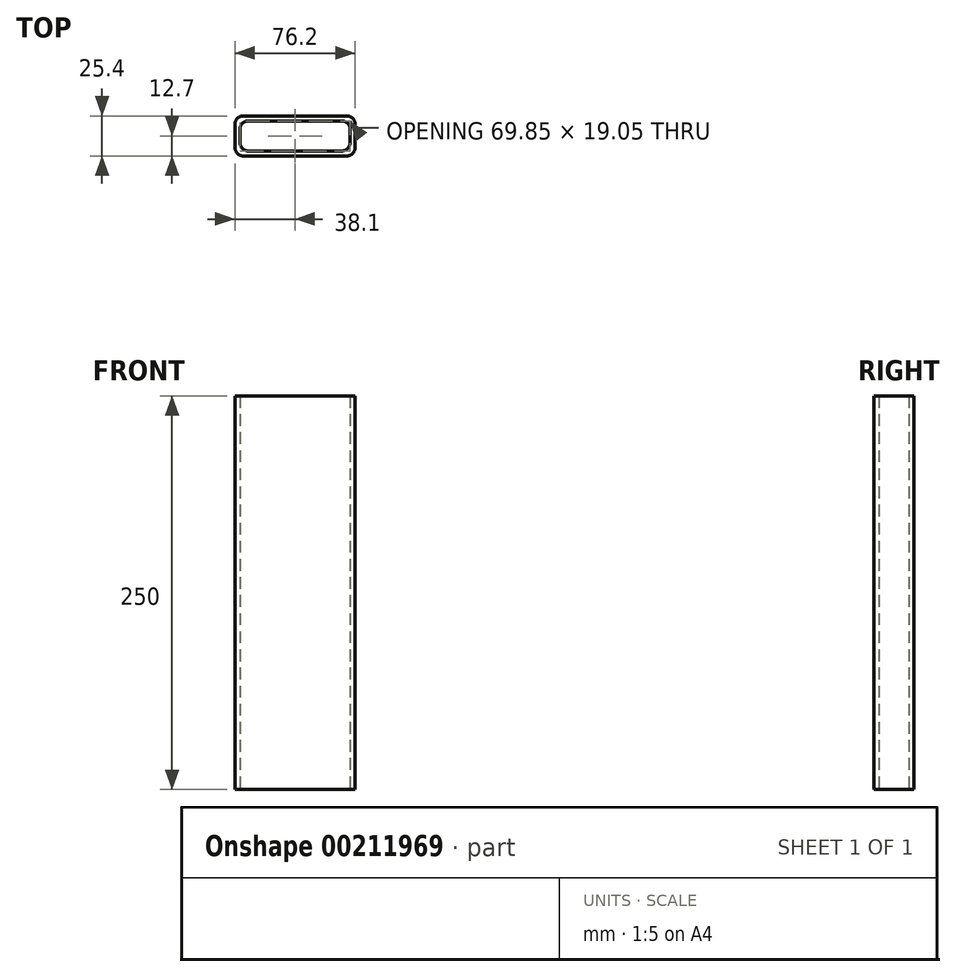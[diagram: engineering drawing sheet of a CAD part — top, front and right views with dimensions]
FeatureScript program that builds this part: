
annotation { "Feature Type Name" : "Feature", "Feature Type Description" : "" }
export const myFeature = defineFeature(function(context is Context, id is Id, definition is map)
    precondition{}
    {
        {
            var Q0;
            Q0=qCreatedBy(makeId("Top.planeOp"),FACE);
            var sketch = newSketch(context, id + "F0", { "sketchPlane" : qUnion([Q0])});
            skLineSegment(sketch, "E0.bottom", {"start": v(38.1, -12.7) * mm, "end": v(-38.1, -12.7) * mm});
            skLineSegment(sketch, "E0.top", {"start": v(38.1, 12.7) * mm, "end": v(-38.1, 12.7) * mm});
            skLineSegment(sketch, "E0.left", {"start": v(38.1, -12.7) * mm, "end": v(38.1, 12.7) * mm});
            skLineSegment(sketch, "E0.right", {"start": v(-38.1, -12.7) * mm, "end": v(-38.1, 12.7) * mm});
            skPoint(sketch, "E0.middle", {"position": v(0, 0) * mm});
            skLineSegment(sketch, "E1.bottom", {"start": v(34.93, -9.52) * mm, "end": v(-34.93, -9.53) * mm});
            skLineSegment(sketch, "E1.top", {"start": v(34.93, 9.53) * mm, "end": v(-34.93, 9.52) * mm});
            skLineSegment(sketch, "E1.left", {"start": v(34.93, -9.52) * mm, "end": v(34.93, 9.53) * mm});
            skLineSegment(sketch, "E1.right", {"start": v(-34.93, -9.53) * mm, "end": v(-34.93, 9.52) * mm});
            skSolve(sketch);
        }
        {
            var Q0;
            Q0=makeQuery(id+"F0.imprint","IMPRINT",FACE,{"disambiguationData":[TD([[makeQuery(id+"F0.imprint","IMPRINT",EDGE,{"derivedFrom":sQuery(id+"F0.wireOp",EDGE,"E0.bottom")}),-1.0]])]});
            extrude(context, id + "F1", {"entities" : qUnion([Q0]), "depth" : 250 * mm});
        }
        {
            var Q0;
            Q0=makeQuery(id+"F1.opExtrude","SWEPT_EDGE",EDGE,{"disambiguationData":[OSD([sQuery(id+"F0.wireOp",EDGE,"E0.bottom"),sQuery(id+"F0.wireOp",EDGE,"E0.left")])]});
            var Q1;
            Q1=makeQuery(id+"F1.opExtrude","SWEPT_EDGE",EDGE,{"disambiguationData":[OSD([sQuery(id+"F0.wireOp",EDGE,"E0.top"),sQuery(id+"F0.wireOp",EDGE,"E0.left")])]});
            var Q2;
            Q2=makeQuery(id+"F1.opExtrude","SWEPT_EDGE",EDGE,{"disambiguationData":[OSD([sQuery(id+"F0.wireOp",EDGE,"E0.bottom"),sQuery(id+"F0.wireOp",EDGE,"E0.right")])]});
            var Q3;
            Q3=makeQuery(id+"F1.opExtrude","SWEPT_EDGE",EDGE,{"disambiguationData":[OSD([sQuery(id+"F0.wireOp",EDGE,"E0.top"),sQuery(id+"F0.wireOp",EDGE,"E0.right")])]});
            fillet(context, id + "F2", {"entities" : qUnion([Q0, Q1, Q2, Q3]), "radius" : 5.08 * mm, "tangentPropagation" : true, "allowEdgeOverflow" : false});
        }
        {
            var Q0;
            Q0=makeQuery(id+"F1.opExtrude","SWEPT_EDGE",EDGE,{"disambiguationData":[OSD([sQuery(id+"F0.wireOp",EDGE,"E1.top"),sQuery(id+"F0.wireOp",EDGE,"E1.left")])]});
            var Q1;
            Q1=makeQuery(id+"F1.opExtrude","SWEPT_EDGE",EDGE,{"disambiguationData":[OSD([sQuery(id+"F0.wireOp",EDGE,"E1.top"),sQuery(id+"F0.wireOp",EDGE,"E1.right")])]});
            var Q2;
            Q2=makeQuery(id+"F1.opExtrude","SWEPT_EDGE",EDGE,{"disambiguationData":[OSD([sQuery(id+"F0.wireOp",EDGE,"E1.bottom"),sQuery(id+"F0.wireOp",EDGE,"E1.left")])]});
            var Q3;
            Q3=makeQuery(id+"F1.opExtrude","SWEPT_EDGE",EDGE,{"disambiguationData":[OSD([sQuery(id+"F0.wireOp",EDGE,"E1.bottom"),sQuery(id+"F0.wireOp",EDGE,"E1.right")])]});
            fillet(context, id + "F3", {"entities" : qUnion([Q0, Q1, Q2, Q3]), "radius" : 5.08 * mm, "tangentPropagation" : true, "allowEdgeOverflow" : false});
        }
    });
